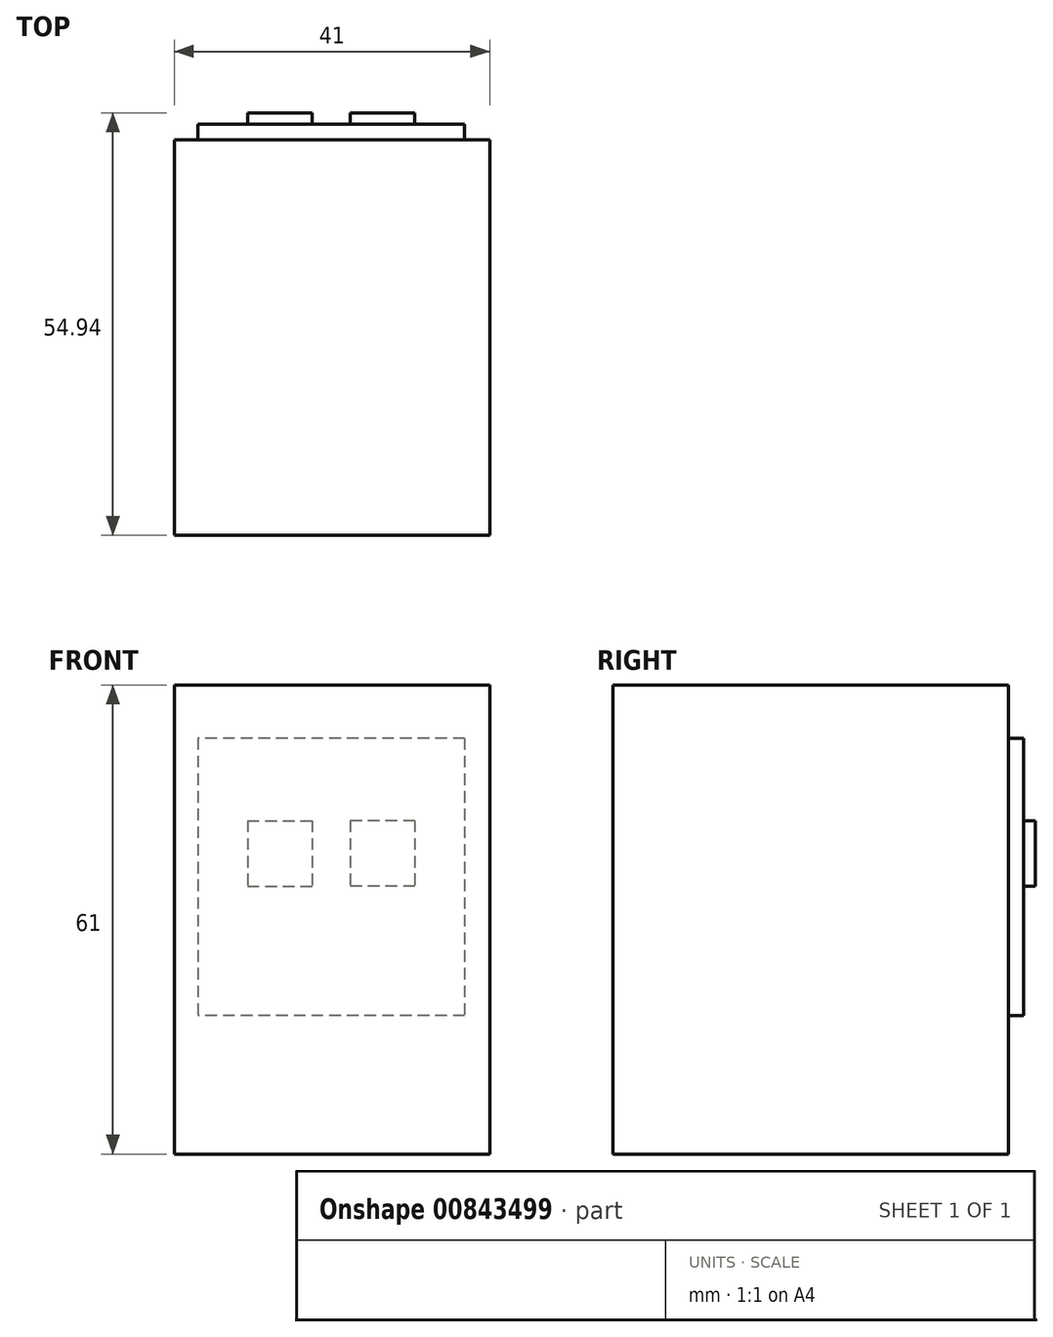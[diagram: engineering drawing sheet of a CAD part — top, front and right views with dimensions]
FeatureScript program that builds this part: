
annotation { "Feature Type Name" : "Feature", "Feature Type Description" : "" }
export const myFeature = defineFeature(function(context is Context, id is Id, definition is map)
    precondition{}
    {
        {
            var Q0;
            Q0=qCreatedBy(makeId("Top.planeOp"),FACE);
            var sketch = newSketch(context, id + "F0", { "sketchPlane" : qUnion([Q0])});
            skLineSegment(sketch, "E0", {"start": v(33.96, -5.25) * mm, "end": v(-7.04, -5.25) * mm});
            skLineSegment(sketch, "E1", {"start": v(33.96, -56.69) * mm, "end": v(-7.04, -56.69) * mm});
            skPoint(sketch, "E2.orphan", {"position": v(-27.47, 74.66) * mm});
            skPoint(sketch, "E3.start.orphan", {"position": v(-27.47, 46.2) * mm});
            skLineSegment(sketch, "E4", {"start": v(33.96, -56.69) * mm, "end": v(33.96, -5.25) * mm});
            skLineSegment(sketch, "E5", {"start": v(-7.04, -5.25) * mm, "end": v(-7.04, -56.69) * mm});
            skSolve(sketch);
        }
        {
            var Q0;
            Q0=makeQuery(id+"F0.imprint","IMPRINT",FACE,{"disambiguationData":[TD([[makeQuery(id+"F0.imprint","IMPRINT",EDGE,{"derivedFrom":sQuery(id+"F0.wireOp",EDGE,"E0")}),1.0]])]});
            extrude(context, id + "F1", {"entities" : qUnion([Q0]), "depth" : 61 * mm, "offsetDistance" : 25 * mm});
        }
        {
            var Q0;
            Q0=makeQuery(id+"F1.opExtrude","SWEPT_FACE",FACE,{"disambiguationData":[OSD([sQuery(id+"F0.wireOp",EDGE,"E0")])]});
            var sketch = newSketch(context, id + "F2", { "sketchPlane" : qUnion([Q0])});
            skLineSegment(sketch, "E6.bottom", {"start": v(-30.7, 54.1) * mm, "end": v(4, 54.1) * mm});
            skLineSegment(sketch, "E6.top", {"start": v(-30.7, 18.04) * mm, "end": v(4, 18.04) * mm});
            skLineSegment(sketch, "E6.left", {"start": v(-30.7, 54.1) * mm, "end": v(-30.7, 18.04) * mm});
            skLineSegment(sketch, "E6.right", {"start": v(4, 54.1) * mm, "end": v(4, 18.04) * mm});
            skSolve(sketch);
        }
        {
            var Q0;
            Q0=makeQuery(id+"F2.imprint","IMPRINT",FACE,{"disambiguationData":[TD([[makeQuery(id+"F2.imprint","IMPRINT",EDGE,{"derivedFrom":sQuery(id+"F2.wireOp",EDGE,"E6.bottom")}),-1.0]])]});
            extrude(context, id + "F3", {"entities" : qUnion([Q0]), "operationType" : NewBodyOperationType.ADD, "depth" : 2 * mm, "offsetDistance" : 25 * mm});
        }
        {
            var Q0;
            Q0=makeQuery(id+"F3.opExtrude","CAP_FACE",FACE,{"disambiguationData":[OSD([sQuery(id+"F2.wireOp",EDGE,"E6.bottom"),sQuery(id+"F2.wireOp",EDGE,"E6.top"),sQuery(id+"F2.wireOp",EDGE,"E6.left"),sQuery(id+"F2.wireOp",EDGE,"E6.right")])],"isStart":false});
            var sketch = newSketch(context, id + "F4", { "sketchPlane" : qUnion([Q0])});
            skLineSegment(sketch, "E7.bottom", {"start": v(-26.7, 43.37) * mm, "end": v(-24.23, 43.37) * mm});
            skLineSegment(sketch, "E7.top", {"start": v(-26.7, 34.83) * mm, "end": v(-24.23, 34.83) * mm});
            skLineSegment(sketch, "E7.left", {"start": v(-26.7, 43.37) * mm, "end": v(-26.7, 34.83) * mm});
            skLineSegment(sketch, "E7.right", {"start": v(-24.23, 43.37) * mm, "end": v(-24.23, 34.83) * mm});
            skLineSegment(sketch, "E8.bottom", {"start": v(0, 43.37) * mm, "end": v(-2.48, 43.37) * mm});
            skLineSegment(sketch, "E8.top", {"start": v(0, 34.83) * mm, "end": v(-2.48, 34.83) * mm});
            skLineSegment(sketch, "E8.left", {"start": v(0, 43.37) * mm, "end": v(0, 34.83) * mm});
            skLineSegment(sketch, "E8.right", {"start": v(-2.48, 43.37) * mm, "end": v(-2.48, 34.83) * mm});
            skLineSegment(sketch, "E9.bottom", {"start": v(-24.23, 43.37) * mm, "end": v(-15.83, 43.37) * mm});
            skLineSegment(sketch, "E9.top", {"start": v(-24.23, 34.83) * mm, "end": v(-15.83, 34.83) * mm});
            skLineSegment(sketch, "E9.right", {"start": v(-15.83, 43.37) * mm, "end": v(-15.83, 34.83) * mm});
            skLineSegment(sketch, "E10.bottom", {"start": v(-2.48, 43.37) * mm, "end": v(-10.88, 43.37) * mm});
            skLineSegment(sketch, "E10.top", {"start": v(-2.48, 34.83) * mm, "end": v(-10.88, 34.83) * mm});
            skLineSegment(sketch, "E10.right", {"start": v(-10.88, 43.37) * mm, "end": v(-10.88, 34.83) * mm});
            skSolve(sketch);
        }
        {
            var Q0;
            Q0=makeQuery(id+"F4.imprint","IMPRINT",FACE,{"disambiguationData":[TD([[makeQuery(id+"F4.imprint","IMPRINT",EDGE,{"derivedFrom":sQuery(id+"F4.wireOp",EDGE,"E9.bottom")}),-1.0]])]});
            var Q1;
            Q1=makeQuery(id+"F4.imprint","IMPRINT",FACE,{"disambiguationData":[TD([[makeQuery(id+"F4.imprint","IMPRINT",EDGE,{"derivedFrom":sQuery(id+"F4.wireOp",EDGE,"E10.bottom")}),1.0]])]});
            extrude(context, id + "F5", {"entities" : qUnion([Q0, Q1]), "operationType" : NewBodyOperationType.ADD, "depth" : 1.5 * mm, "offsetDistance" : 25 * mm});
        }
    });
